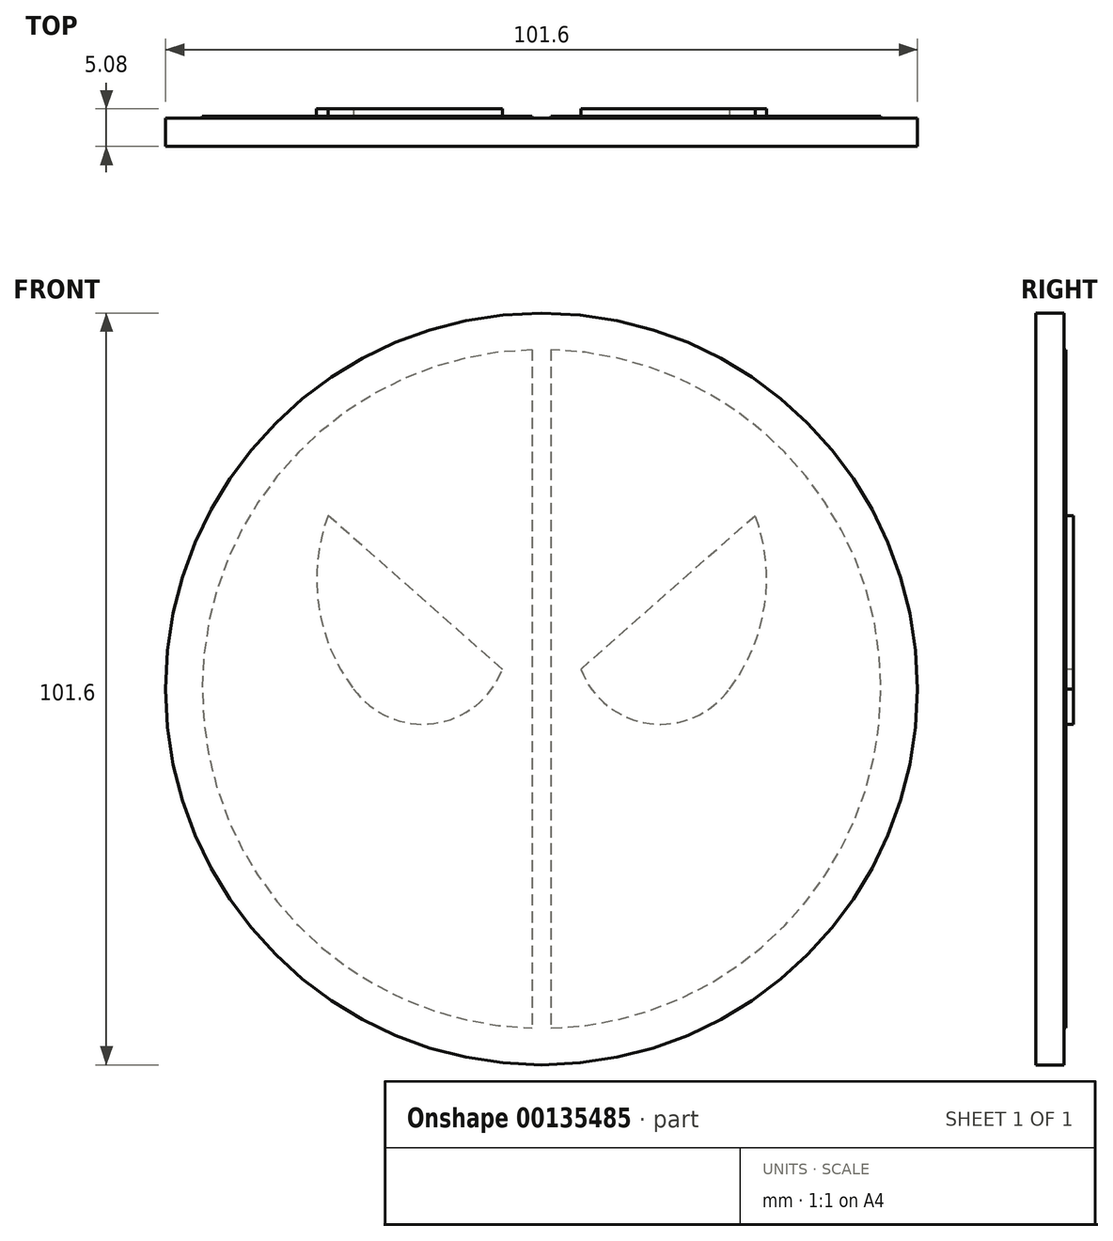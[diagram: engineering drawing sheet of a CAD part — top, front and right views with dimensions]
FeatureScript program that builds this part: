
annotation { "Feature Type Name" : "Feature", "Feature Type Description" : "" }
export const myFeature = defineFeature(function(context is Context, id is Id, definition is map)
    precondition{}
    {
        {
            var Q0;
            Q0=qCreatedBy(makeId("Front.planeOp"),FACE);
            var sketch = newSketch(context, id + "F0", { "sketchPlane" : qUnion([Q0])});
            skCircle(sketch, "E0", {"center": v(0, 0) * mm, "radius": 50.8 * mm});
            skSolve(sketch);
        }
        {
            var Q0;
            Q0 = qSketchRegion(id + "F0", true);
            extrude(context, id + "F1", {"entities" : qUnion([Q0]), "depth" : 3.8 * mm});
        }
        {
            var Q0;
            Q0=qCreatedBy(makeId("Front.planeOp"),FACE);
            var sketch = newSketch(context, id + "F2", { "sketchPlane" : qUnion([Q0])});
            skArc(sketch, "E1", {"start": v(-1.27, 45.84) * mm, "mid": v(-45.85, 0) * mm, "end": v(-1.27, -45.84) * mm});
            skLineSegment(sketch, "E2", {"start": v(1.27, 45.84) * mm, "end": v(1.27, -45.84) * mm});
            skLineSegment(sketch, "E3.MirrorCS", {"start": v(-1.27, 45.84) * mm, "end": v(-1.27, -45.84) * mm});
            skArc(sketch, "E4.trimOffspring", {"start": v(1.27, -45.84) * mm, "mid": v(45.85, 0) * mm, "end": v(1.27, 45.84) * mm});
            skSolve(sketch);
        }
        {
            var Q0;
            Q0 = qSketchRegion(id + "F2", true);
            extrude(context, id + "F3", {"entities" : qUnion([Q0]), "operationType" : NewBodyOperationType.ADD, "oppositeDirection" : true, "depth" : 0.25 * mm});
        }
        {
            var Q0;
            Q0=qCreatedBy(makeId("Front.planeOp"),FACE);
            var sketch = newSketch(context, id + "F4", { "sketchPlane" : qUnion([Q0])});
            skLineSegment(sketch, "E5", {"start": v(-5.3, 2.66) * mm, "end": v(-28.85, 23.44) * mm});
            skArc(sketch, "E6", {"start": v(-25.4, 0) * mm, "mid": v(-14.56, -4.67) * mm, "end": v(-5.3, 2.66) * mm});
            skArc(sketch, "E7", {"start": v(-28.85, 23.44) * mm, "mid": v(-30.14, 11.28) * mm, "end": v(-25.4, 0) * mm});
            skLineSegment(sketch, "E8.MirrorCS", {"start": v(5.3, 2.66) * mm, "end": v(28.85, 23.44) * mm});
            skArc(sketch, "E9.MirrorCS", {"start": v(25.4, 0) * mm, "mid": v(14.56, -4.67) * mm, "end": v(5.3, 2.66) * mm});
            skArc(sketch, "E10.MirrorCS", {"start": v(28.85, 23.44) * mm, "mid": v(30.14, 11.28) * mm, "end": v(25.4, 0) * mm});
            skSolve(sketch);
        }
        {
            var Q0;
            Q0 = qSketchRegion(id + "F4", true);
            extrude(context, id + "F5", {"entities" : qUnion([Q0]), "operationType" : NewBodyOperationType.ADD, "oppositeDirection" : true, "depth" : 1.27 * mm});
        }
    });
